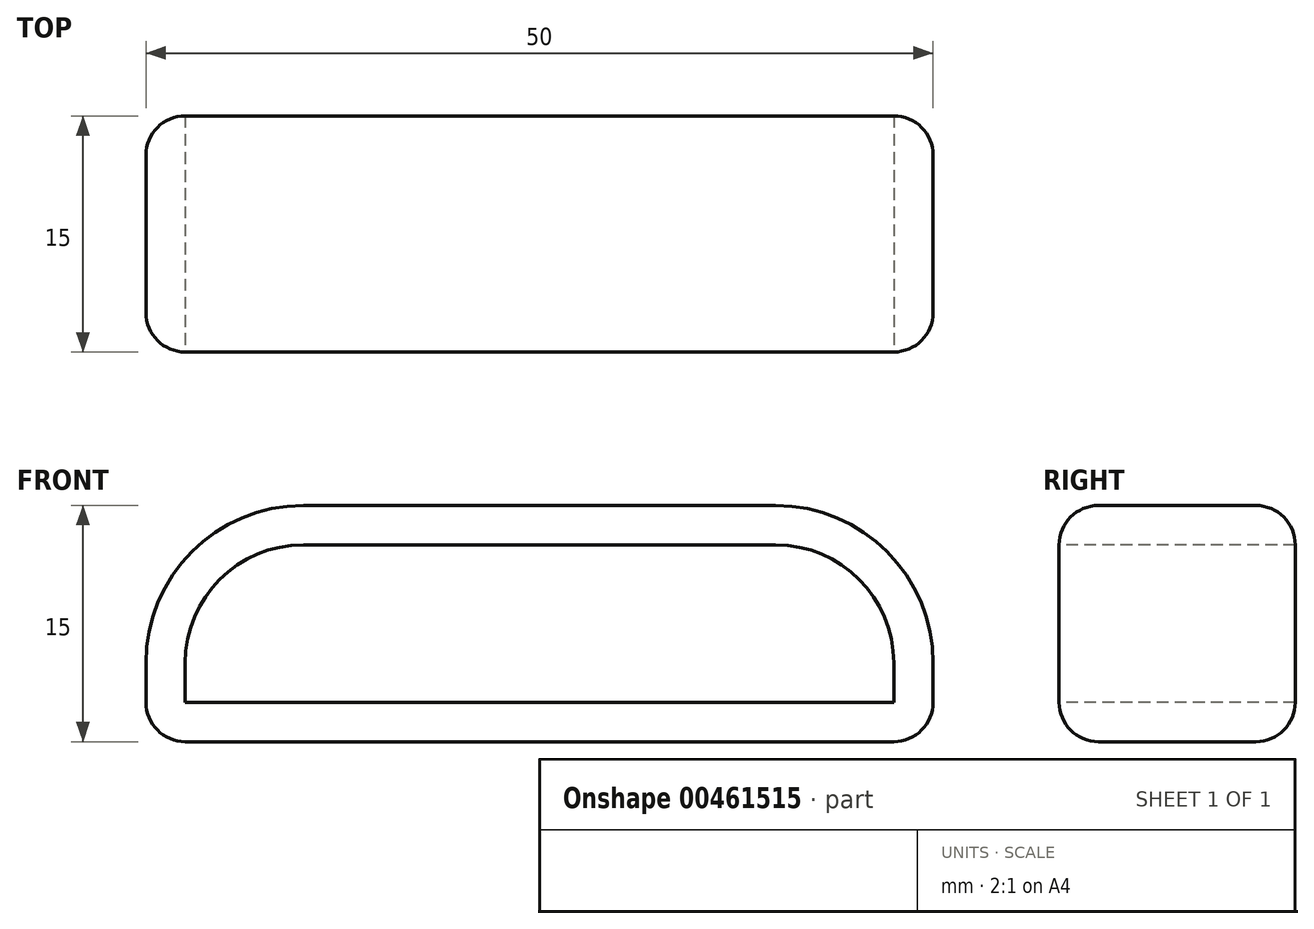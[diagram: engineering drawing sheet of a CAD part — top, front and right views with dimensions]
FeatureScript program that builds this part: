
annotation { "Feature Type Name" : "Feature", "Feature Type Description" : "" }
export const myFeature = defineFeature(function(context is Context, id is Id, definition is map)
    precondition{}
    {
        {
            var Q0;
            Q0=qCreatedBy(makeId("Front.planeOp"),FACE);
            var sketch = newSketch(context, id + "F0", { "sketchPlane" : qUnion([Q0])});
            skLineSegment(sketch, "E0.bottom", {"start": v(-64.43, 15) * mm, "end": v(-34.43, 15) * mm});
            skLineSegment(sketch, "E0.top", {"start": v(-71.93, 0) * mm, "end": v(-26.93, 0) * mm});
            skLineSegment(sketch, "E0.left", {"start": v(-74.43, 5) * mm, "end": v(-74.43, 2.5) * mm});
            skLineSegment(sketch, "E0.right", {"start": v(-24.43, 5) * mm, "end": v(-24.43, 2.5) * mm});
            skPoint(sketch, "E1.visualSharp", {"position": v(-74.43, 15) * mm});
            skArc(sketch, "E1.filletArc", {"start": v(-64.43, 15) * mm, "mid": v(-71.5, 12.07) * mm, "end": v(-74.43, 5) * mm});
            skPoint(sketch, "E2.visualSharp", {"position": v(-24.43, 15) * mm});
            skArc(sketch, "E2.filletArc", {"start": v(-24.43, 5) * mm, "mid": v(-27.36, 12.07) * mm, "end": v(-34.43, 15) * mm});
            skPoint(sketch, "E3.visualSharp", {"position": v(-24.43, 0) * mm});
            skArc(sketch, "E3.filletArc", {"start": v(-26.93, 0) * mm, "mid": v(-25.16, 0.73) * mm, "end": v(-24.43, 2.5) * mm});
            skPoint(sketch, "E4.visualSharp", {"position": v(-74.43, 0) * mm});
            skArc(sketch, "E4.filletArc", {"start": v(-74.43, 2.5) * mm, "mid": v(-73.7, 0.73) * mm, "end": v(-71.93, 0) * mm});
            skLineSegment(sketch, "E5", {"start": v(-74.43, 5) * mm, "end": v(-24.43, 5) * mm});
            skSolve(sketch);
        }
        {
            var Q0;
            Q0 = qSketchRegion(id + "F0", true);
            extrude(context, id + "F1", {"entities" : qUnion([Q0]), "depth" : 15 * mm});
        }
        {
            var Q0;
            Q0=makeQuery(id+"F1.opExtrude","SWEPT_FACE",FACE,{"disambiguationData":[OSD([sQuery(id+"F0.wireOp",EDGE,"E1.filletArc")])]});
            fillet(context, id + "F2", {"entities" : qUnion([Q0]), "radius" : 2.5 * mm, "tangentPropagation" : true, "allowEdgeOverflow" : false});
        }
        {
            var Q0;
            Q0=makeQuery(id+"F1.opExtrude","CAP_FACE",FACE,{"disambiguationData":[OSD([sQuery(id+"F0.wireOp",EDGE,"E0.bottom"),sQuery(id+"F0.wireOp",EDGE,"E0.top"),sQuery(id+"F0.wireOp",EDGE,"E0.left"),sQuery(id+"F0.wireOp",EDGE,"E0.right"),sQuery(id+"F0.wireOp",EDGE,"E1.filletArc"),sQuery(id+"F0.wireOp",EDGE,"E2.filletArc"),sQuery(id+"F0.wireOp",EDGE,"E3.filletArc"),sQuery(id+"F0.wireOp",EDGE,"E4.filletArc")])],"isStart":false});
            var sketch = newSketch(context, id + "F3", { "sketchPlane" : qUnion([Q0])});
            skSolve(sketch);
        }
        {
            var Q0;
            {var subQ0=sQuery(id+"F0.wireOp",EDGE,"E2.filletArc");var subQ1=sQuery(id+"F0.wireOp",EDGE,"E1.filletArc");var subQ2=sQuery(id+"F0.wireOp",EDGE,"E0.right");var subQ3=sQuery(id+"F0.wireOp",EDGE,"E0.left");var subQ4=sQuery(id+"F0.wireOp",EDGE,"E0.top");var subQ5=sQuery(id+"F0.wireOp",EDGE,"E0.bottom");var subQ6=makeQuery(id+"F1.opExtrude","CAP_FACE",FACE,{"disambiguationData":[OSD([subQ5,subQ4,subQ3,subQ2,subQ1,subQ0,sQuery(id+"F0.wireOp",EDGE,"E3.filletArc"),sQuery(id+"F0.wireOp",EDGE,"E4.filletArc")])],"isStart":false});Q0=makeQuery(id+"F3.imprint","IMPRINT",FACE,{"disambiguationData":[TD([[makeQuery(id+"F3.imprint","IMPRINT",EDGE,{"derivedFrom":makeQuery(id+"F2.opFillet","BLEND_EDGE",EDGE,{"blendedFrom":[makeQuery(id+"F1.opExtrude","CAP_EDGE",EDGE,{"disambiguationData":[OSD([subQ5])],"isStart":false}),subQ6],"blendedInto":[subQ6]})}),1.0]])]});}
            extrude(context, id + "F4", {"entities" : qUnion([Q0]), "operationType" : NewBodyOperationType.REMOVE, "endBound" : BoundingType.THROUGH_ALL, "oppositeDirection" : true, "depth" : 25 * mm});
        }
    });
